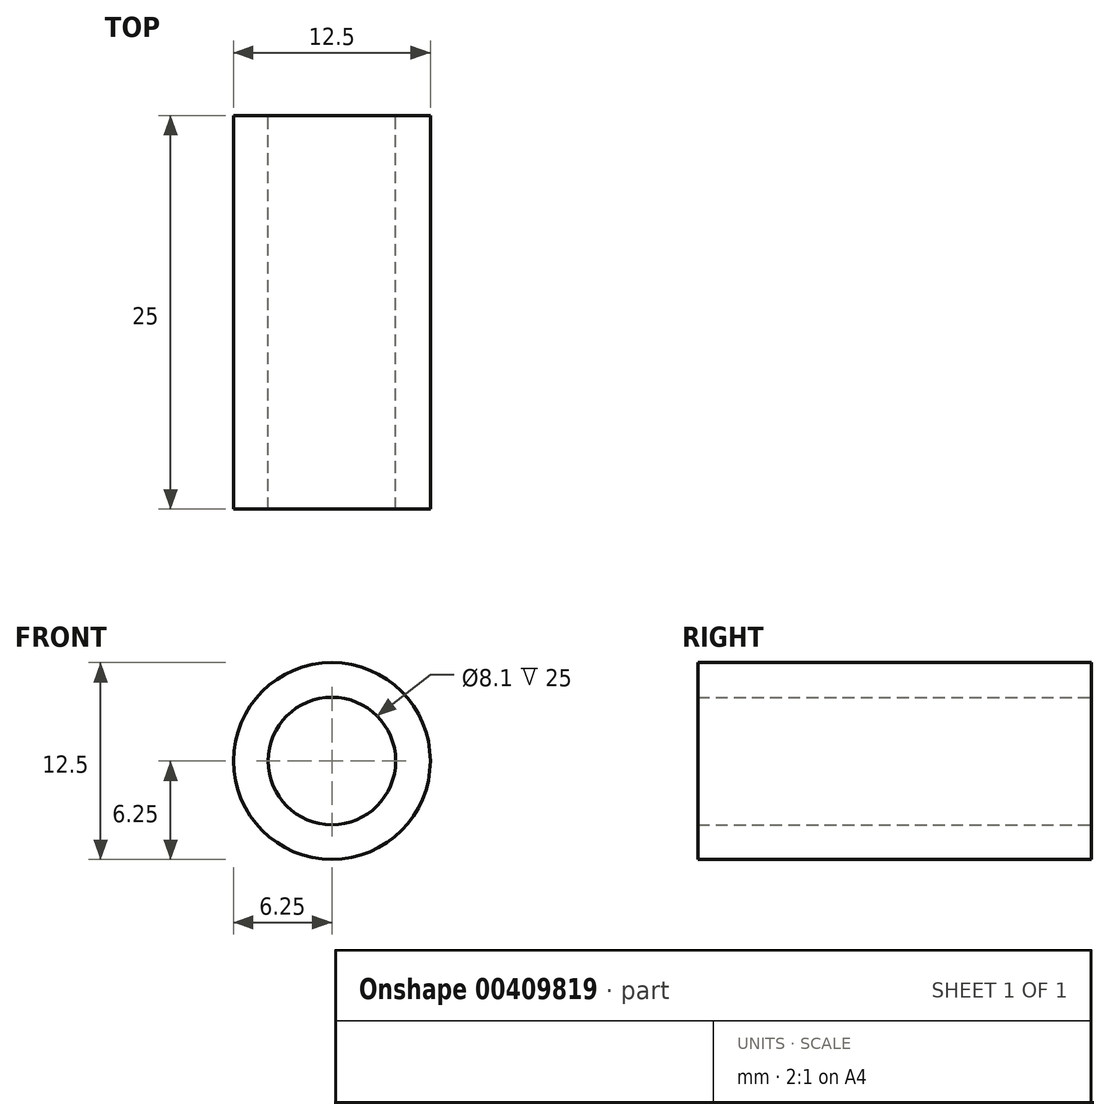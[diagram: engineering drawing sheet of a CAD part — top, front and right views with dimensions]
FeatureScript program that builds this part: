
annotation { "Feature Type Name" : "Feature", "Feature Type Description" : "" }
export const myFeature = defineFeature(function(context is Context, id is Id, definition is map)
    precondition{}
    {
        {
            var Q0;
            Q0=qCreatedBy(makeId("Front.planeOp"),FACE);
            var sketch = newSketch(context, id + "F0", { "sketchPlane" : qUnion([Q0])});
            skCircle(sketch, "E0", {"center": v(0, 0) * mm, "radius": 4.05 * mm});
            skCircle(sketch, "E1.0", {"center": v(0, 0) * mm, "radius": 6.25 * mm});
            skSolve(sketch);
        }
        {
            var Q0;
            Q0 = qSketchRegion(id + "F0", true);
            extrude(context, id + "F1", {"entities" : qUnion([Q0]), "depth" : 25 * mm});
        }
    });
